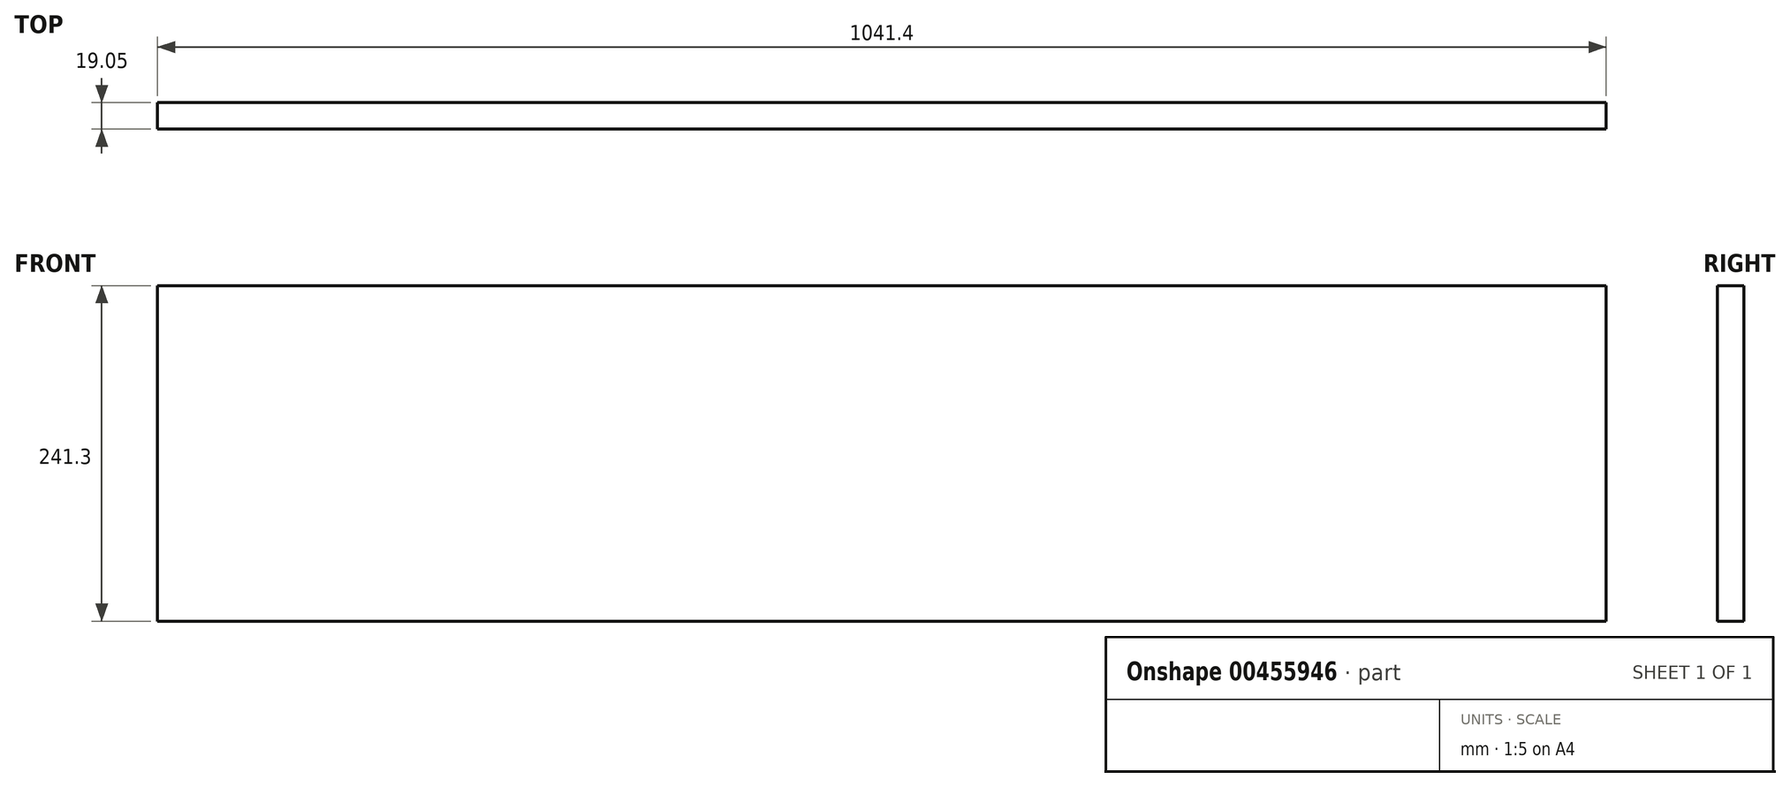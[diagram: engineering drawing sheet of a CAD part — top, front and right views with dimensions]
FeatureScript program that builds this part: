
annotation { "Feature Type Name" : "Feature", "Feature Type Description" : "" }
export const myFeature = defineFeature(function(context is Context, id is Id, definition is map)
    precondition{}
    {
        {
            var Q0;
            Q0=qCreatedBy(makeId("Front.planeOp"),FACE);
            var sketch = newSketch(context, id + "F0", { "sketchPlane" : qUnion([Q0])});
            skLineSegment(sketch, "E0.bottom", {"start": v(-293.42, 142.7) * mm, "end": v(747.98, 142.7) * mm});
            skLineSegment(sketch, "E0.top", {"start": v(-293.42, -98.6) * mm, "end": v(747.98, -98.6) * mm});
            skLineSegment(sketch, "E0.left", {"start": v(-293.42, 142.7) * mm, "end": v(-293.42, -98.6) * mm});
            skLineSegment(sketch, "E0.right", {"start": v(747.98, 142.7) * mm, "end": v(747.98, -98.6) * mm});
            skSolve(sketch);
        }
        {
            var Q0;
            Q0=makeQuery(id+"F0.imprint","IMPRINT",FACE,{"disambiguationData":[TD([[makeQuery(id+"F0.imprint","IMPRINT",EDGE,{"derivedFrom":sQuery(id+"F0.wireOp",EDGE,"E0.bottom")}),-1.0]])]});
            extrude(context, id + "F1", {"entities" : qUnion([Q0]), "depth" : 19.05 * mm, "offsetDistance" : 25.4 * mm});
        }
    });
